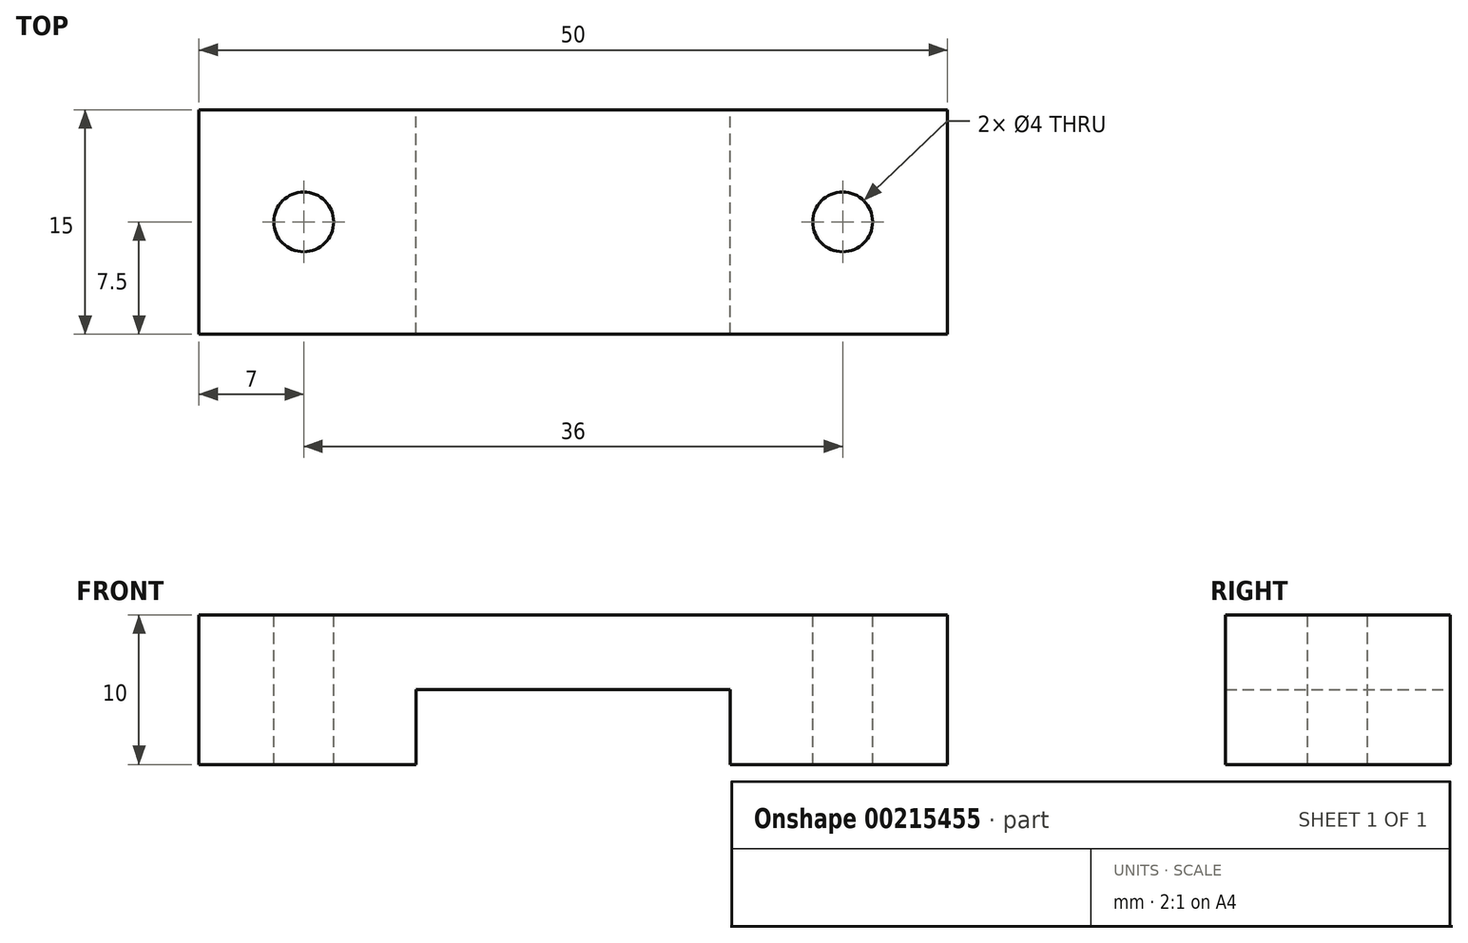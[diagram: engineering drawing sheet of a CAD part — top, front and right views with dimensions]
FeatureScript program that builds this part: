
annotation { "Feature Type Name" : "Feature", "Feature Type Description" : "" }
export const myFeature = defineFeature(function(context is Context, id is Id, definition is map)
    precondition{}
    {
        {
            var Q0;
            Q0=qCreatedBy(makeId("Front.planeOp"),FACE);
            var sketch = newSketch(context, id + "F0", { "sketchPlane" : qUnion([Q0])});
            skLineSegment(sketch, "E0", {"start": v(-25, 0) * mm, "end": v(25, 0) * mm});
            skLineSegment(sketch, "E1", {"start": v(-25, 0) * mm, "end": v(-25, -10) * mm});
            skLineSegment(sketch, "E2", {"start": v(25, 0) * mm, "end": v(25, -10) * mm});
            skLineSegment(sketch, "E3", {"start": v(-25, -10) * mm, "end": v(-10.5, -10) * mm});
            skLineSegment(sketch, "E4", {"start": v(25, -10) * mm, "end": v(10.5, -10) * mm});
            skLineSegment(sketch, "E5", {"start": v(-10.5, -10) * mm, "end": v(-10.5, -5) * mm});
            skLineSegment(sketch, "E6", {"start": v(10.5, -10) * mm, "end": v(10.5, -5) * mm});
            skLineSegment(sketch, "E7", {"start": v(-10.5, -5) * mm, "end": v(10.5, -5) * mm});
            skSolve(sketch);
        }
        {
            var Q0;
            Q0 = qSketchRegion(id + "F0", true);
            extrude(context, id + "F1", {"entities" : qUnion([Q0]), "depth" : 15 * mm});
        }
        {
            var Q0;
            Q0=qCreatedBy(makeId("Top.planeOp"),FACE);
            var sketch = newSketch(context, id + "F2", { "sketchPlane" : qUnion([Q0])});
            skCircle(sketch, "E8", {"center": v(-18, -7.5) * mm, "radius": 2 * mm});
            skCircle(sketch, "E9", {"center": v(18, -7.5) * mm, "radius": 2 * mm});
            skSolve(sketch);
        }
        {
            var Q0;
            Q0 = qSketchRegion(id + "F2", true);
            extrude(context, id + "F3", {"entities" : qUnion([Q0]), "operationType" : NewBodyOperationType.REMOVE, "oppositeDirection" : true, "depth" : 25 * mm});
        }
    });
